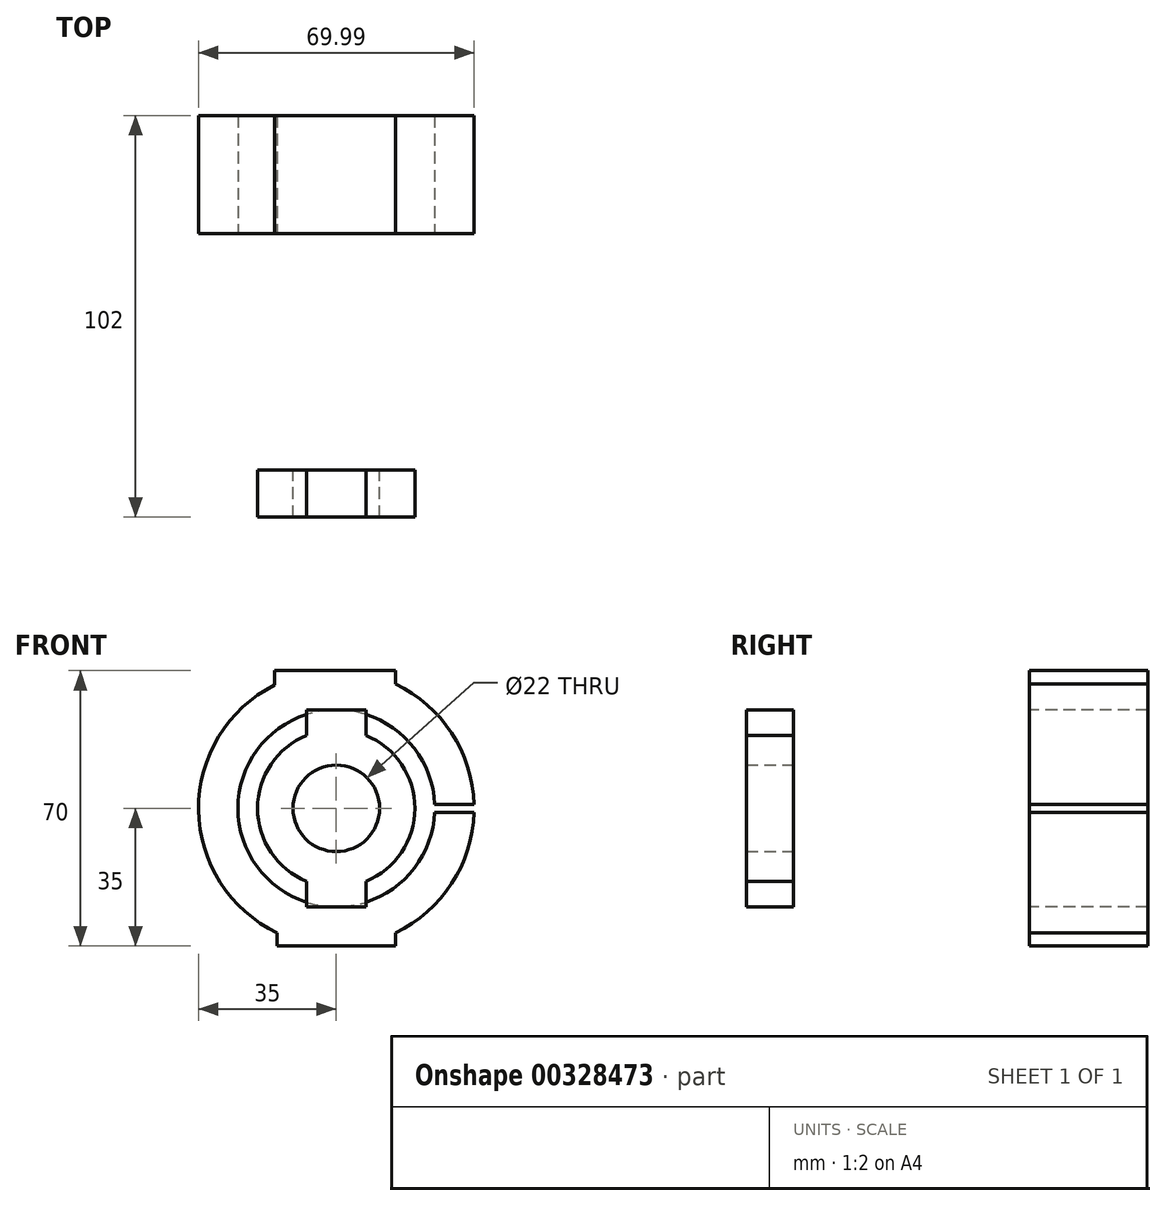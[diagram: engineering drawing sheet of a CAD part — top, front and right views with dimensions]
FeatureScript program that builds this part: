
annotation { "Feature Type Name" : "Feature", "Feature Type Description" : "" }
export const myFeature = defineFeature(function(context is Context, id is Id, definition is map)
    precondition{}
    {
        {
            var Q0;
            Q0=qCreatedBy(makeId("Front.planeOp"),FACE);
            var sketch = newSketch(context, id + "F0", { "sketchPlane" : qUnion([Q0])});
            skCircle(sketch, "E0", {"center": v(0, 0) * mm, "radius": 11 * mm});
            skCircle(sketch, "E1", {"center": v(0, 0) * mm, "radius": 20 * mm});
            skSolve(sketch);
        }
        {
            var Q0;
            Q0=makeQuery(id+"F0.imprint","IMPRINT",FACE,{"disambiguationData":[TD([[makeQuery(id+"F0.imprint","IMPRINT",EDGE,{"derivedFrom":sQuery(id+"F0.wireOp",EDGE,"E0")}),-1.0]])]});
            extrude(context, id + "F1", {"entities" : qUnion([Q0]), "depth" : 12 * mm});
        }
        {
            var Q0;
            Q0=qCreatedBy(makeId("Front.planeOp"),FACE);
            cPlane(context, id + "F2", {"entities" : qUnion([Q0]), "cplaneType" : CPlaneType.OFFSET, "offset" : 60 * mm, "oppositeDirection" : true, "width" : 150 * mm, "height" : 150 * mm});
        }
        {
            var Q0;
            Q0=qCreatedBy(id+"F2.planeOp",FACE);
            var sketch = newSketch(context, id + "F3", { "sketchPlane" : qUnion([Q0])});
            skCircle(sketch, "E2", {"center": v(0, 0) * mm, "radius": 25 * mm});
            skCircle(sketch, "E3", {"center": v(0, 0) * mm, "radius": 35 * mm});
            skSolve(sketch);
        }
        {
            var Q0;
            Q0=makeQuery(id+"F3.imprint","IMPRINT",FACE,{"disambiguationData":[TD([[makeQuery(id+"F3.imprint","IMPRINT",EDGE,{"derivedFrom":sQuery(id+"F3.wireOp",EDGE,"E2")}),-1.0]])]});
            extrude(context, id + "F4", {"entities" : qUnion([Q0]), "oppositeDirection" : true, "depth" : 30 * mm});
        }
        {
            var Q0;
            Q0=makeQuery(id+"F4.opExtrude","CAP_FACE",FACE,{"disambiguationData":[OSD([sQuery(id+"F3.wireOp",EDGE,"E2"),sQuery(id+"F3.wireOp",EDGE,"E3")])],"isStart":false});
            var sketch = newSketch(context, id + "F5", { "sketchPlane" : qUnion([Q0])});
            skLineSegment(sketch, "E4", {"start": v(0, 0) * mm, "end": v(-35, 0) * mm, "construction": true});
            skLineSegment(sketch, "E5", {"start": v(-35, 0) * mm, "end": v(-35, -1) * mm});
            skLineSegment(sketch, "E6", {"start": v(-35, -1) * mm, "end": v(-22.58, -1) * mm});
            skLineSegment(sketch, "E7", {"start": v(-22.58, -1) * mm, "end": v(-22.58, 1) * mm});
            skLineSegment(sketch, "E8", {"start": v(-22.58, 1) * mm, "end": v(-35, 1) * mm});
            skLineSegment(sketch, "E9", {"start": v(-35, 1) * mm, "end": v(-35, 0) * mm});
            skSolve(sketch);
        }
        {
            var Q0;
            {var subQ0=sQuery(id+"F5.wireOp",EDGE,"E5");Q0=makeQuery(id+"F5.imprint","IMPRINT",FACE,{"disambiguationData":[TD([[makeQuery(id+"F5.imprint","IMPRINT",EDGE,{"derivedFrom":subQ0}),1.0]])]});}
            var Q1;
            {var subQ0=sQuery(id+"F5.wireOp",EDGE,"E9");Q1=makeQuery(id+"F5.imprint","IMPRINT",FACE,{"disambiguationData":[TD([[makeQuery(id+"F5.imprint","IMPRINT",EDGE,{"derivedFrom":subQ0}),1.0]])]});}
            var Q2;
            {var subQ0=sQuery(id+"F5.wireOp",EDGE,"E7");Q2=makeQuery(id+"F5.imprint","IMPRINT",FACE,{"disambiguationData":[TD([[makeQuery(id+"F5.imprint","IMPRINT",EDGE,{"derivedFrom":subQ0}),1.0]])]});}
            var Q3;
            {var subQ0=sQuery(id+"F5.wireOp",EDGE,"E6");var subQ5=makeQuery(id+"F4.opExtrude","CAP_EDGE",EDGE,{"disambiguationData":[OSD([sQuery(id+"F3.wireOp",EDGE,"E3")])],"isStart":false});var subQ8=makeQuery(id+"F5.imprint","INTERSECT",VERTEX,{"derivedFrom":[subQ5,subQ0]});Q3=makeQuery(id+"F5.imprint","IMPRINT",FACE,{"disambiguationData":[TD([[makeQuery(id+"F5.imprint","IMPRINT",EDGE,{"disambiguationData":[TD([[subQ8,-1.0]])],"derivedFrom":subQ0}),1.0]])]});}
            extrude(context, id + "F6", {"entities" : qUnion([Q0, Q1, Q2, Q3]), "operationType" : NewBodyOperationType.REMOVE, "oppositeDirection" : true, "depth" : 30 * mm});
        }
        {
            var Q0;
            Q0=qCreatedBy(makeId("Top.planeOp"),FACE);
            cPlane(context, id + "F7", {"entities" : qUnion([Q0]), "cplaneType" : CPlaneType.OFFSET, "offset" : 20 * mm, "width" : 150 * mm, "height" : 150 * mm});
        }
        {
            var Q0;
            Q0=qCreatedBy(makeId("Top.planeOp"),FACE);
            cPlane(context, id + "F8", {"entities" : qUnion([Q0]), "cplaneType" : CPlaneType.OFFSET, "offset" : 20 * mm, "oppositeDirection" : true, "width" : 150 * mm, "height" : 150 * mm});
        }
        {
            var Q0;
            Q0=qCreatedBy(id+"F7.planeOp",FACE);
            var sketch = newSketch(context, id + "F9", { "sketchPlane" : qUnion([Q0])});
            skLineSegment(sketch, "E10", {"start": v(0, 0) * mm, "end": v(-7.5, 0) * mm});
            skLineSegment(sketch, "E11", {"start": v(-7.5, 0) * mm, "end": v(-7.5, -12) * mm});
            skLineSegment(sketch, "E12", {"start": v(-7.5, -12) * mm, "end": v(0, -12) * mm});
            skLineSegment(sketch, "E13", {"start": v(0, -12) * mm, "end": v(7.5, -12) * mm});
            skLineSegment(sketch, "E14", {"start": v(7.5, -12) * mm, "end": v(7.5, 0) * mm});
            skLineSegment(sketch, "E15", {"start": v(7.5, 0) * mm, "end": v(0, 0) * mm});
            skSolve(sketch);
        }
        {
            var Q0;
            Q0=makeQuery(id+"F9.imprint","IMPRINT",FACE,{"disambiguationData":[TD([[makeQuery(id+"F9.imprint","IMPRINT",EDGE,{"derivedFrom":sQuery(id+"F9.wireOp",EDGE,"E10")}),1.0]])]});
            extrude(context, id + "F10", {"entities" : qUnion([Q0]), "operationType" : NewBodyOperationType.ADD, "oppositeDirection" : true, "depth" : 3 * mm});
        }
        {
            var Q0;
            Q0=makeQuery(id+"F10.opExtrude","CAP_FACE",FACE,{"disambiguationData":[OSD([sQuery(id+"F9.wireOp",EDGE,"E10"),sQuery(id+"F9.wireOp",EDGE,"E11"),sQuery(id+"F9.wireOp",EDGE,"E12"),sQuery(id+"F9.wireOp",EDGE,"E13"),sQuery(id+"F9.wireOp",EDGE,"E14"),sQuery(id+"F9.wireOp",EDGE,"E15")])],"isStart":true});
            extrude(context, id + "F11", {"entities" : qUnion([Q0]), "operationType" : NewBodyOperationType.ADD, "depth" : 5 * mm});
        }
        {
            var Q0;
            Q0=qCreatedBy(id+"F8.planeOp",FACE);
            var sketch = newSketch(context, id + "F12", { "sketchPlane" : qUnion([Q0])});
            skLineSegment(sketch, "E16", {"start": v(0, 0) * mm, "end": v(7.5, 0) * mm});
            skLineSegment(sketch, "E17", {"start": v(7.5, 0) * mm, "end": v(7.5, -12) * mm});
            skLineSegment(sketch, "E18", {"start": v(7.5, -12) * mm, "end": v(0, -12) * mm});
            skLineSegment(sketch, "E19", {"start": v(0, -12) * mm, "end": v(-7.5, -12) * mm});
            skLineSegment(sketch, "E20", {"start": v(-7.5, -12) * mm, "end": v(-7.5, 0) * mm});
            skLineSegment(sketch, "E21", {"start": v(-7.5, 0) * mm, "end": v(0, 0) * mm});
            skSolve(sketch);
        }
        {
            var Q0;
            Q0=makeQuery(id+"F12.imprint","IMPRINT",FACE,{"disambiguationData":[TD([[makeQuery(id+"F12.imprint","IMPRINT",EDGE,{"derivedFrom":sQuery(id+"F12.wireOp",EDGE,"E16")}),-1.0]])]});
            extrude(context, id + "F13", {"entities" : qUnion([Q0]), "operationType" : NewBodyOperationType.ADD, "depth" : 3 * mm});
        }
        {
            var Q0;
            Q0=makeQuery(id+"F13.opExtrude","CAP_FACE",FACE,{"disambiguationData":[OSD([sQuery(id+"F12.wireOp",EDGE,"E16"),sQuery(id+"F12.wireOp",EDGE,"E17"),sQuery(id+"F12.wireOp",EDGE,"E18"),sQuery(id+"F12.wireOp",EDGE,"E19"),sQuery(id+"F12.wireOp",EDGE,"E20"),sQuery(id+"F12.wireOp",EDGE,"E21")])],"isStart":true});
            extrude(context, id + "F14", {"entities" : qUnion([Q0]), "operationType" : NewBodyOperationType.ADD, "depth" : 5 * mm});
        }
        {
            var Q0;
            Q0=qCreatedBy(id+"F7.planeOp",FACE);
            cPlane(context, id + "F15", {"entities" : qUnion([Q0]), "cplaneType" : CPlaneType.OFFSET, "offset" : 15 * mm, "width" : 150 * mm, "height" : 150 * mm});
        }
        {
            var Q0;
            Q0=qCreatedBy(id+"F8.planeOp",FACE);
            cPlane(context, id + "F16", {"entities" : qUnion([Q0]), "cplaneType" : CPlaneType.OFFSET, "offset" : 15 * mm, "oppositeDirection" : true, "width" : 150 * mm, "height" : 150 * mm});
        }
        {
            var Q0;
            Q0=qCreatedBy(id+"F16.planeOp",FACE);
            var sketch = newSketch(context, id + "F17", { "sketchPlane" : qUnion([Q0])});
            skLineSegment(sketch, "E22", {"start": v(0, 0) * mm, "end": v(0, 60) * mm, "construction": true});
            skLineSegment(sketch, "E23", {"start": v(0, 60) * mm, "end": v(-15, 60) * mm});
            skLineSegment(sketch, "E24", {"start": v(-15, 60) * mm, "end": v(-15, 90) * mm});
            skLineSegment(sketch, "E25", {"start": v(-15, 90) * mm, "end": v(0, 90) * mm});
            skLineSegment(sketch, "E26", {"start": v(15, 90) * mm, "end": v(15, 60) * mm});
            skLineSegment(sketch, "E27", {"start": v(15, 60) * mm, "end": v(0, 60) * mm});
            skLineSegment(sketch, "E28", {"start": v(0, 90) * mm, "end": v(15, 90) * mm});
            skSolve(sketch);
        }
        {
            var Q0;
            Q0=makeQuery(id+"F17.imprint","IMPRINT",FACE,{"disambiguationData":[TD([[makeQuery(id+"F17.imprint","IMPRINT",EDGE,{"derivedFrom":sQuery(id+"F17.wireOp",EDGE,"E23")}),-1.0]])]});
            extrude(context, id + "F18", {"entities" : qUnion([Q0]), "operationType" : NewBodyOperationType.ADD, "depth" : 5 * mm});
        }
        {
            var Q0;
            Q0=qCreatedBy(id+"F15.planeOp",FACE);
            var sketch = newSketch(context, id + "F19", { "sketchPlane" : qUnion([Q0])});
            skLineSegment(sketch, "E29", {"start": v(0, 0) * mm, "end": v(0, 60) * mm});
            skLineSegment(sketch, "E30", {"start": v(0, 60) * mm, "end": v(15, 60) * mm});
            skLineSegment(sketch, "E31", {"start": v(15, 60) * mm, "end": v(15, 90) * mm});
            skLineSegment(sketch, "E32", {"start": v(15, 90) * mm, "end": v(0, 90) * mm});
            skLineSegment(sketch, "E33", {"start": v(0, 90) * mm, "end": v(-15.66, 90) * mm});
            skLineSegment(sketch, "E34", {"start": v(-15.66, 90) * mm, "end": v(-15.66, 60) * mm});
            skLineSegment(sketch, "E35", {"start": v(-15.66, 60) * mm, "end": v(0, 60) * mm});
            skSolve(sketch);
        }
        {
            var Q0;
            Q0=makeQuery(id+"F19.imprint","IMPRINT",FACE,{"disambiguationData":[TD([[makeQuery(id+"F19.imprint","IMPRINT",EDGE,{"derivedFrom":sQuery(id+"F19.wireOp",EDGE,"E30")}),1.0]])]});
            extrude(context, id + "F20", {"entities" : qUnion([Q0]), "operationType" : NewBodyOperationType.ADD, "oppositeDirection" : true, "depth" : 5 * mm});
        }
    });
